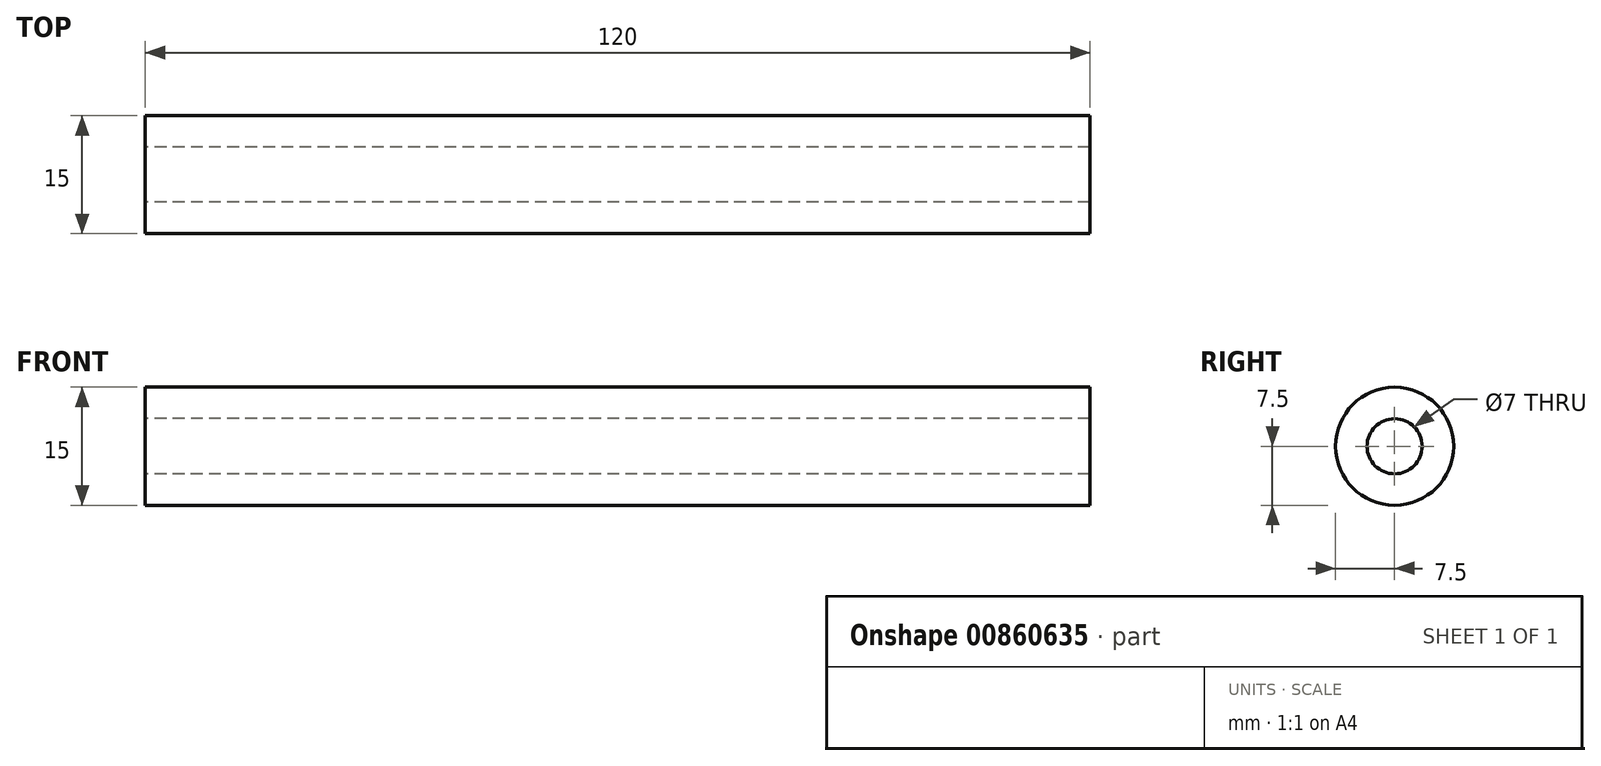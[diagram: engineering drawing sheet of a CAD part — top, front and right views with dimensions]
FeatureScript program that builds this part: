
annotation { "Feature Type Name" : "Feature", "Feature Type Description" : "" }
export const myFeature = defineFeature(function(context is Context, id is Id, definition is map)
    precondition{}
    {
        {
            var Q0;
            Q0=qCreatedBy(makeId("Right.planeOp"),FACE);
            cPlane(context, id + "F0", {"entities" : qUnion([Q0]), "cplaneType" : CPlaneType.OFFSET, "offset" : 20 * mm, "width" : 150 * mm, "height" : 150 * mm});
        }
        {
            var Q0;
            Q0=qCreatedBy(id+"F0.planeOp",FACE);
            var sketch = newSketch(context, id + "F1", { "sketchPlane" : qUnion([Q0])});
            skCircle(sketch, "E0", {"center": v(0, 0) * mm, "radius": 7.5 * mm});
            skCircle(sketch, "E1", {"center": v(0, 0) * mm, "radius": 3.5 * mm});
            skSolve(sketch);
        }
        {
            var Q0;
            Q0 = qSketchRegion(id + "F1", true);
            extrude(context, id + "F2", {"entities" : qUnion([Q0]), "depth" : 120 * mm, "offsetDistance" : 25 * mm});
        }
    });
